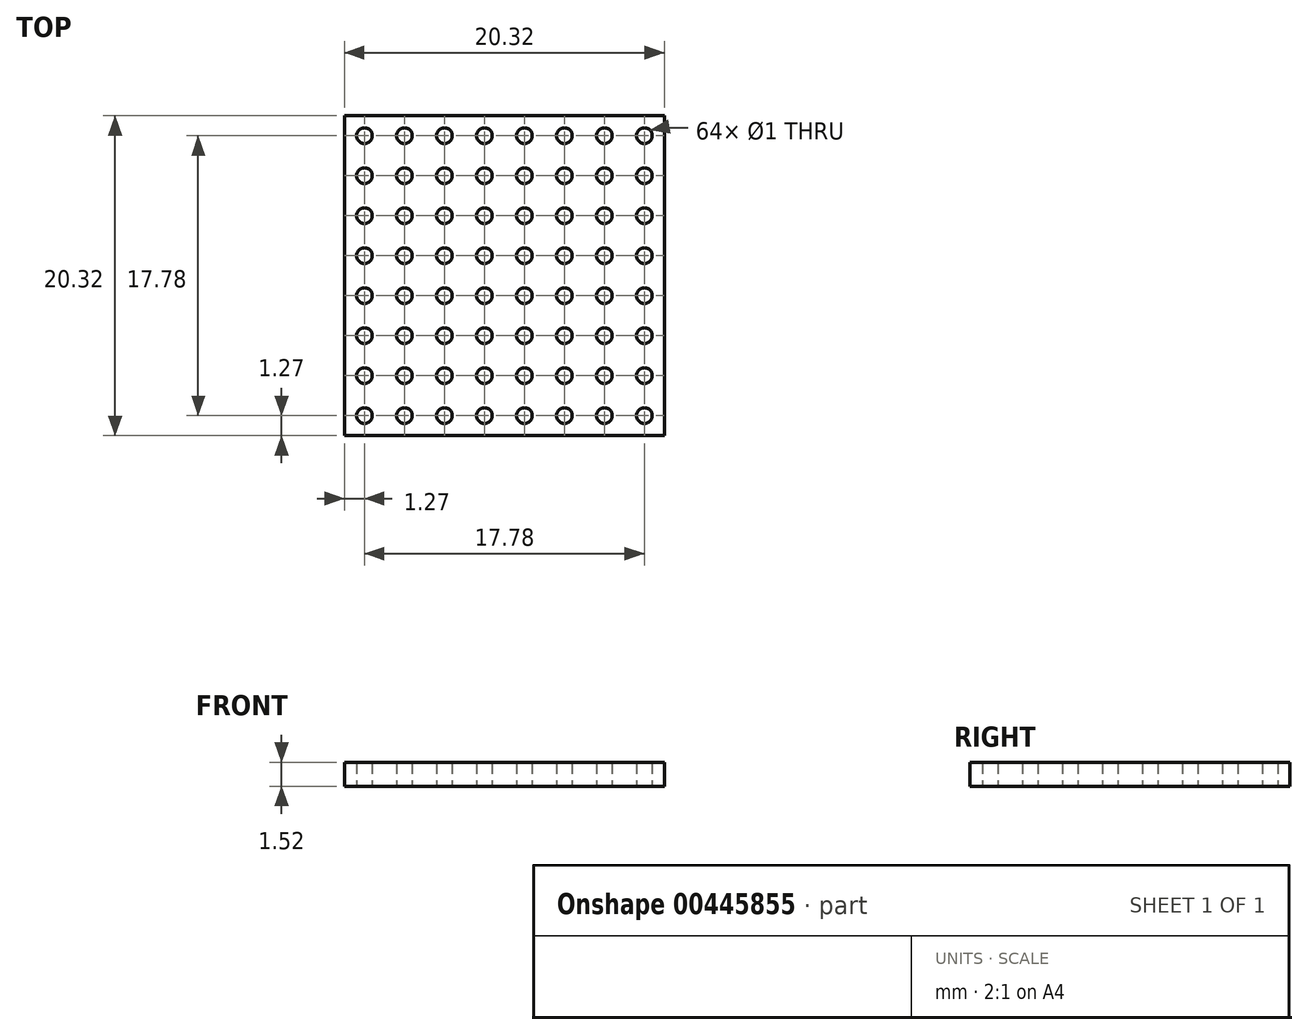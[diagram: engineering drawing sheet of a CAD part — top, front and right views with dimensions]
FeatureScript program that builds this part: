
annotation { "Feature Type Name" : "Feature", "Feature Type Description" : "" }
export const myFeature = defineFeature(function(context is Context, id is Id, definition is map)
    precondition{}
    {
        {
            var Q0;
            Q0=qCreatedBy(makeId("Top.planeOp"),FACE);
            var sketch = newSketch(context, id + "F0", { "sketchPlane" : qUnion([Q0])});
            skCircle(sketch, "E0", {"center": v(0, 0) * mm, "radius": 0.5 * mm});
            skCircle(sketch, "E1.0.1.0", {"center": v(0, 2.54) * mm, "radius": 0.5 * mm});
            skCircle(sketch, "E1.0.2.0", {"center": v(0, 5.08) * mm, "radius": 0.5 * mm});
            skCircle(sketch, "E1.0.3.0", {"center": v(0, 7.62) * mm, "radius": 0.5 * mm});
            skCircle(sketch, "E1.0.4.0", {"center": v(0, 10.16) * mm, "radius": 0.5 * mm});
            skCircle(sketch, "E1.0.5.0", {"center": v(0, 12.7) * mm, "radius": 0.5 * mm});
            skCircle(sketch, "E1.0.6.0", {"center": v(0, 15.24) * mm, "radius": 0.5 * mm});
            skCircle(sketch, "E1.0.7.0", {"center": v(0, 17.78) * mm, "radius": 0.5 * mm});
            skCircle(sketch, "E1.1.0.0", {"center": v(2.54, 0) * mm, "radius": 0.5 * mm});
            skCircle(sketch, "E1.1.1.0", {"center": v(2.54, 2.54) * mm, "radius": 0.5 * mm});
            skCircle(sketch, "E1.1.2.0", {"center": v(2.54, 5.08) * mm, "radius": 0.5 * mm});
            skCircle(sketch, "E1.1.3.0", {"center": v(2.54, 7.62) * mm, "radius": 0.5 * mm});
            skCircle(sketch, "E1.1.4.0", {"center": v(2.54, 10.16) * mm, "radius": 0.5 * mm});
            skCircle(sketch, "E1.1.5.0", {"center": v(2.54, 12.7) * mm, "radius": 0.5 * mm});
            skCircle(sketch, "E1.1.6.0", {"center": v(2.54, 15.24) * mm, "radius": 0.5 * mm});
            skCircle(sketch, "E1.1.7.0", {"center": v(2.54, 17.78) * mm, "radius": 0.5 * mm});
            skCircle(sketch, "E1.2.0.0", {"center": v(5.08, 0) * mm, "radius": 0.5 * mm});
            skCircle(sketch, "E1.2.1.0", {"center": v(5.08, 2.54) * mm, "radius": 0.5 * mm});
            skCircle(sketch, "E1.2.2.0", {"center": v(5.08, 5.08) * mm, "radius": 0.5 * mm});
            skCircle(sketch, "E1.2.3.0", {"center": v(5.08, 7.62) * mm, "radius": 0.5 * mm});
            skCircle(sketch, "E1.2.4.0", {"center": v(5.08, 10.16) * mm, "radius": 0.5 * mm});
            skCircle(sketch, "E1.2.5.0", {"center": v(5.08, 12.7) * mm, "radius": 0.5 * mm});
            skCircle(sketch, "E1.2.6.0", {"center": v(5.08, 15.24) * mm, "radius": 0.5 * mm});
            skCircle(sketch, "E1.2.7.0", {"center": v(5.08, 17.78) * mm, "radius": 0.5 * mm});
            skCircle(sketch, "E1.3.0.0", {"center": v(7.62, 0) * mm, "radius": 0.5 * mm});
            skCircle(sketch, "E1.3.1.0", {"center": v(7.62, 2.54) * mm, "radius": 0.5 * mm});
            skCircle(sketch, "E1.3.2.0", {"center": v(7.62, 5.08) * mm, "radius": 0.5 * mm});
            skCircle(sketch, "E1.3.3.0", {"center": v(7.62, 7.62) * mm, "radius": 0.5 * mm});
            skCircle(sketch, "E1.3.4.0", {"center": v(7.62, 10.16) * mm, "radius": 0.5 * mm});
            skCircle(sketch, "E1.3.5.0", {"center": v(7.62, 12.7) * mm, "radius": 0.5 * mm});
            skCircle(sketch, "E1.3.6.0", {"center": v(7.62, 15.24) * mm, "radius": 0.5 * mm});
            skCircle(sketch, "E1.3.7.0", {"center": v(7.62, 17.78) * mm, "radius": 0.5 * mm});
            skCircle(sketch, "E1.4.0.0", {"center": v(10.16, 0) * mm, "radius": 0.5 * mm});
            skCircle(sketch, "E1.4.1.0", {"center": v(10.16, 2.54) * mm, "radius": 0.5 * mm});
            skCircle(sketch, "E1.4.2.0", {"center": v(10.16, 5.08) * mm, "radius": 0.5 * mm});
            skCircle(sketch, "E1.4.3.0", {"center": v(10.16, 7.62) * mm, "radius": 0.5 * mm});
            skCircle(sketch, "E1.4.4.0", {"center": v(10.16, 10.16) * mm, "radius": 0.5 * mm});
            skCircle(sketch, "E1.4.5.0", {"center": v(10.16, 12.7) * mm, "radius": 0.5 * mm});
            skCircle(sketch, "E1.4.6.0", {"center": v(10.16, 15.24) * mm, "radius": 0.5 * mm});
            skCircle(sketch, "E1.4.7.0", {"center": v(10.16, 17.78) * mm, "radius": 0.5 * mm});
            skCircle(sketch, "E1.5.0.0", {"center": v(12.7, 0) * mm, "radius": 0.5 * mm});
            skCircle(sketch, "E1.5.1.0", {"center": v(12.7, 2.54) * mm, "radius": 0.5 * mm});
            skCircle(sketch, "E1.5.2.0", {"center": v(12.7, 5.08) * mm, "radius": 0.5 * mm});
            skCircle(sketch, "E1.5.3.0", {"center": v(12.7, 7.62) * mm, "radius": 0.5 * mm});
            skCircle(sketch, "E1.5.4.0", {"center": v(12.7, 10.16) * mm, "radius": 0.5 * mm});
            skCircle(sketch, "E1.5.5.0", {"center": v(12.7, 12.7) * mm, "radius": 0.5 * mm});
            skCircle(sketch, "E1.5.6.0", {"center": v(12.7, 15.24) * mm, "radius": 0.5 * mm});
            skCircle(sketch, "E1.5.7.0", {"center": v(12.7, 17.78) * mm, "radius": 0.5 * mm});
            skCircle(sketch, "E1.6.0.0", {"center": v(15.24, 0) * mm, "radius": 0.5 * mm});
            skCircle(sketch, "E1.6.1.0", {"center": v(15.24, 2.54) * mm, "radius": 0.5 * mm});
            skCircle(sketch, "E1.6.2.0", {"center": v(15.24, 5.08) * mm, "radius": 0.5 * mm});
            skCircle(sketch, "E1.6.3.0", {"center": v(15.24, 7.62) * mm, "radius": 0.5 * mm});
            skCircle(sketch, "E1.6.4.0", {"center": v(15.24, 10.16) * mm, "radius": 0.5 * mm});
            skCircle(sketch, "E1.6.5.0", {"center": v(15.24, 12.7) * mm, "radius": 0.5 * mm});
            skCircle(sketch, "E1.6.6.0", {"center": v(15.24, 15.24) * mm, "radius": 0.5 * mm});
            skCircle(sketch, "E1.6.7.0", {"center": v(15.24, 17.78) * mm, "radius": 0.5 * mm});
            skCircle(sketch, "E1.7.0.0", {"center": v(17.78, 0) * mm, "radius": 0.5 * mm});
            skCircle(sketch, "E1.7.1.0", {"center": v(17.78, 2.54) * mm, "radius": 0.5 * mm});
            skCircle(sketch, "E1.7.2.0", {"center": v(17.78, 5.08) * mm, "radius": 0.5 * mm});
            skCircle(sketch, "E1.7.3.0", {"center": v(17.78, 7.62) * mm, "radius": 0.5 * mm});
            skCircle(sketch, "E1.7.4.0", {"center": v(17.78, 10.16) * mm, "radius": 0.5 * mm});
            skCircle(sketch, "E1.7.5.0", {"center": v(17.78, 12.7) * mm, "radius": 0.5 * mm});
            skCircle(sketch, "E1.7.6.0", {"center": v(17.78, 15.24) * mm, "radius": 0.5 * mm});
            skCircle(sketch, "E1.7.7.0", {"center": v(17.78, 17.78) * mm, "radius": 0.5 * mm});
            skLineSegment(sketch, "E1.direction1", {"start": v(0, 0) * mm, "end": v(2.54, 0) * mm, "construction": true});
            skLineSegment(sketch, "E1.direction2", {"start": v(0, 0) * mm, "end": v(0, 2.54) * mm, "construction": true});
            skLineSegment(sketch, "E2.bottom", {"start": v(-1.27, -1.27) * mm, "end": v(19.05, -1.27) * mm});
            skLineSegment(sketch, "E2.top", {"start": v(-1.27, 19.05) * mm, "end": v(19.05, 19.05) * mm});
            skLineSegment(sketch, "E2.left", {"start": v(-1.27, -1.27) * mm, "end": v(-1.27, 19.05) * mm});
            skLineSegment(sketch, "E2.right", {"start": v(19.05, -1.27) * mm, "end": v(19.05, 19.05) * mm});
            skSolve(sketch);
        }
        {
            var Q0;
            Q0=makeQuery(id+"F0.imprint","IMPRINT",FACE,{"disambiguationData":[TD([[makeQuery(id+"F0.imprint","IMPRINT",EDGE,{"derivedFrom":sQuery(id+"F0.wireOp",EDGE,"E0")}),-1.0]])]});
            extrude(context, id + "F1", {"entities" : qUnion([Q0]), "depth" : 1.52 * mm});
        }
    });
